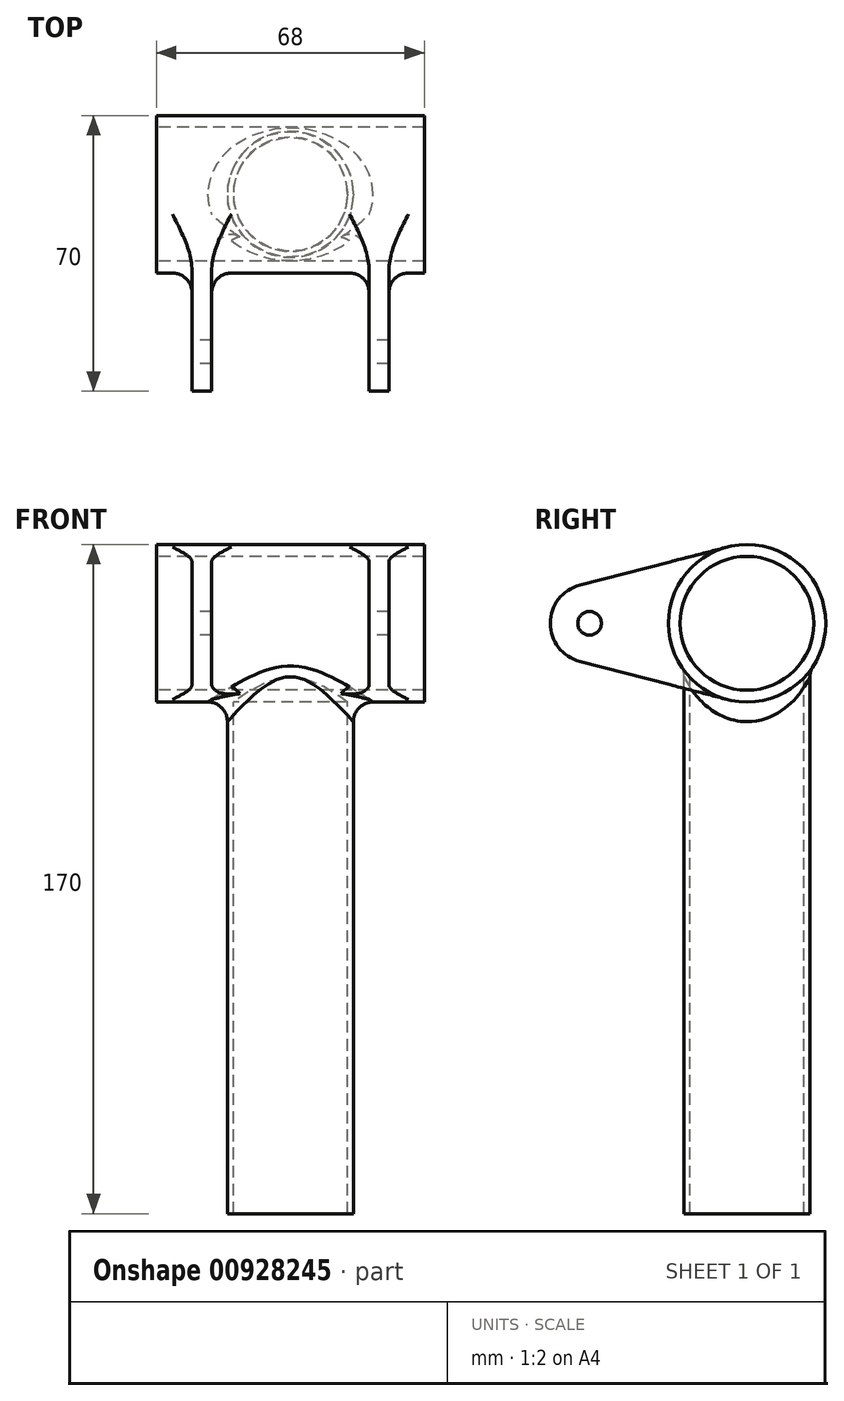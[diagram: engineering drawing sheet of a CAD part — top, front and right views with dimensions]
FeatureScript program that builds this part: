
annotation { "Feature Type Name" : "Feature", "Feature Type Description" : "" }
export const myFeature = defineFeature(function(context is Context, id is Id, definition is map)
    precondition{}
    {
        {
            var Q0;
            Q0=qCreatedBy(makeId("Right.planeOp"),FACE);
            var sketch = newSketch(context, id + "F0", { "sketchPlane" : qUnion([Q0])});
            skCircle(sketch, "E0", {"center": v(0, 0) * mm, "radius": 20 * mm});
            skSolve(sketch);
        }
        {
            var Q0;
            Q0=qCreatedBy(makeId("Top.planeOp"),FACE);
            var sketch = newSketch(context, id + "F1", { "sketchPlane" : qUnion([Q0])});
            skCircle(sketch, "E1", {"center": v(0, 0) * mm, "radius": 16 * mm});
            skSolve(sketch);
        }
        {
            var Q0;
            Q0=qCreatedBy(makeId("Right.planeOp"),FACE);
            var sketch = newSketch(context, id + "F2", { "sketchPlane" : qUnion([Q0])});
            skArc(sketch, "E2", {"start": v(-5, 19.36) * mm, "mid": v(-20, 0) * mm, "end": v(-5, -19.36) * mm});
            skArc(sketch, "E3", {"start": v(-42.5, 9.68) * mm, "mid": v(-50, 0) * mm, "end": v(-42.5, -9.68) * mm});
            skLineSegment(sketch, "E4", {"start": v(-42.5, 9.68) * mm, "end": v(-5, 19.36) * mm});
            skLineSegment(sketch, "E5", {"start": v(-42.5, -9.68) * mm, "end": v(-5, -19.36) * mm});
            skCircle(sketch, "E6", {"center": v(-40, 0) * mm, "radius": 3 * mm});
            skSolve(sketch);
        }
        {
            var Q0;
            Q0=qCreatedBy(makeId("Right.planeOp"),FACE);
            var sketch = newSketch(context, id + "F3", { "sketchPlane" : qUnion([Q0])});
            skArc(sketch, "E7.0", {"start": v(-5, 19.36) * mm, "mid": v(-20, 0) * mm, "end": v(-5, -19.36) * mm});
            skArc(sketch, "E7.1", {"start": v(-42.5, 9.68) * mm, "mid": v(-50, 0) * mm, "end": v(-42.5, -9.68) * mm});
            skLineSegment(sketch, "E7.2", {"start": v(-42.5, 9.68) * mm, "end": v(-5, 19.36) * mm});
            skLineSegment(sketch, "E7.3", {"start": v(-42.5, -9.68) * mm, "end": v(-5, -19.36) * mm});
            skSolve(sketch);
        }
        {
            var Q0;
            Q0=qCreatedBy(makeId("Top.planeOp"),FACE);
            var sketch = newSketch(context, id + "F4", { "sketchPlane" : qUnion([Q0])});
            skCircle(sketch, "E8", {"center": v(0, 0) * mm, "radius": 14.5 * mm});
            skSolve(sketch);
        }
        {
            var Q0;
            Q0=qCreatedBy(makeId("Right.planeOp"),FACE);
            var sketch = newSketch(context, id + "F5", { "sketchPlane" : qUnion([Q0])});
            skCircle(sketch, "E9", {"center": v(0, 0) * mm, "radius": 17 * mm});
            skSolve(sketch);
        }
        {
            var Q0;
            Q0=makeQuery(id+"F2.imprint","IMPRINT",FACE,{"disambiguationData":[TD([[makeQuery(id+"F2.imprint","IMPRINT",EDGE,{"derivedFrom":sQuery(id+"F2.wireOp",EDGE,"E2")}),-1.0]])]});
            extrude(context, id + "F6", {"entities" : qUnion([Q0]), "endBound" : BoundingType.SYMMETRIC, "depth" : 50 * mm, "offsetDistance" : 25 * mm});
        }
        {
            var Q0;
            Q0=qSketchRegion(id+"F3",true);
            extrude(context, id + "F7", {"entities" : qUnion([Q0]), "operationType" : NewBodyOperationType.REMOVE, "endBound" : BoundingType.SYMMETRIC, "depth" : 40 * mm, "offsetDistance" : 25 * mm});
        }
        {
            var Q0;
            Q0=qSketchRegion(id+"F1",true);
            extrude(context, id + "F8", {"entities" : qUnion([Q0]), "oppositeDirection" : true, "depth" : 150 * mm, "offsetDistance" : 25 * mm});
        }
        {
            var Q0;
            Q0=qSketchRegion(id+"F4",true);
            extrude(context, id + "F9", {"entities" : qUnion([Q0]), "operationType" : NewBodyOperationType.REMOVE, "oppositeDirection" : true, "depth" : 150 * mm, "offsetDistance" : 25 * mm});
        }
        {
            var Q0;
            Q0=makeQuery(id+"F0.imprint","IMPRINT",FACE,{"disambiguationData":[TD([[makeQuery(id+"F0.imprint","IMPRINT",EDGE,{"derivedFrom":sQuery(id+"F0.wireOp",EDGE,"E0")}),1.0]])]});
            extrude(context, id + "F10", {"entities" : qUnion([Q0]), "operationType" : NewBodyOperationType.ADD, "endBound" : BoundingType.SYMMETRIC, "depth" : 68 * mm, "offsetDistance" : 25 * mm});
        }
        {
            var Q0;
            Q0=qSketchRegion(id+"F5",true);
            extrude(context, id + "F11", {"entities" : qUnion([Q0]), "operationType" : NewBodyOperationType.REMOVE, "endBound" : BoundingType.SYMMETRIC, "depth" : 68 * mm, "offsetDistance" : 25 * mm});
        }
        {
            var Q0;
            Q0=makeQuery(id+"F10.boolean.opBoolean","INTERSECT",EDGE,{"derivedFrom":[makeQuery(id+"F8.opExtrude","SWEPT_FACE",FACE,{"disambiguationData":[OSD([sQuery(id+"F1.wireOp",EDGE,"E1")])]}),makeQuery(id+"F10.opExtrude","SWEPT_FACE",FACE,{"disambiguationData":[OSD([sQuery(id+"F0.wireOp",EDGE,"E0")])]})]});
            fillet(context, id + "F12", {"entities" : qUnion([Q0]), "radius" : 5 * mm, "tangentPropagation" : true});
        }
        {
            var Q0;
            Q0=makeQuery(id+"F7.boolean.opBoolean","COPY",EDGE,{"derivedFrom":makeQuery(id+"F7.opExtrude","CAP_EDGE",EDGE,{"disambiguationData":[OSD([sQuery(id+"F3.wireOp",EDGE,"E7.0")])],"isStart":true})});
            var Q1;
            Q1=makeQuery(id+"F6.opExtrude","CAP_EDGE",EDGE,{"disambiguationData":[OSD([sQuery(id+"F2.wireOp",EDGE,"E2")])],"isStart":false});
            var Q2;
            Q2=makeQuery(id+"F7.boolean.opBoolean","COPY",EDGE,{"derivedFrom":makeQuery(id+"F7.opExtrude","CAP_EDGE",EDGE,{"disambiguationData":[OSD([sQuery(id+"F3.wireOp",EDGE,"E7.0")])],"isStart":false})});
            var Q3;
            Q3=makeQuery(id+"F6.opExtrude","CAP_EDGE",EDGE,{"disambiguationData":[OSD([sQuery(id+"F2.wireOp",EDGE,"E2")])],"isStart":true});
            fillet(context, id + "F13", {"entities" : qUnion([Q0, Q1, Q2, Q3]), "radius" : 5 * mm, "tangentPropagation" : true});
        }
    });
